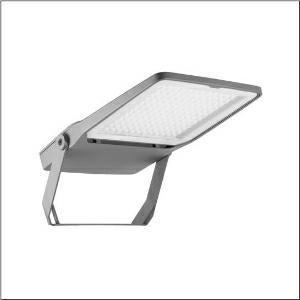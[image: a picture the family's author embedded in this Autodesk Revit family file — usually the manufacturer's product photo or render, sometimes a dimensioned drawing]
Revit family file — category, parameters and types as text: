
# Revit family: floodlight_fl_20_midi___pl61_5xa7682d2c1ac_8fda
name_source: partatom
category: Lighting Fixtures
units: mm (PartAtom-declared; Revit-internal decimal feet)

## family parameters
Cut with Voids When Loaded = No
Host = Face
Light Source = No
Part Type = Normal
Room Calculation Point = No
Round Connector Dimension = Use Diameter
Shared = No

## types (1)
- --- (1 x LED 4000K / CRI = 70 (unbekannt), 18200 lm, 4000K)
    Apparent Load = 142 VA
    CIE Flux Codes = 33 65 98 100 100
    Color Rendering = 70
    Color Temperature = 4000K
    Default Elevation = 1800 mm
    Description = Floodlight FL 20 midi, floodlight, primary light control with lens, of plastic, primary optical cover: protective disc, of toughened safety glass, transparent, light distribution: PL61, light emission: direct distribution, primary light characteristic: asymmetric, installation type: surface-mounted, LED High Power LED, rated luminous flux: 18.200 lm, light colour: 740, colour temperature: 4000K, control gear: ECG Plus, control: flexible luminous flux parameterisation, time-dependent luminous flux control, digital communication interface, power reduction, overheat protection, electronic power reduction, with terminal, 5-pole, max. 2.5mm², mains connection: 220..240V, AC, 50/60Hz, rated input power: 142W, LED unit, of diecast aluminium, powder-coated, Siteco® metallic grey (DB 702S), length: 654 mm, width: 450 mm, height: 76mm, housing frame, of diecast aluminium, powder-coated, Siteco® metallic grey (DB 702S), mounting bracket, of steel, powder-coated, Siteco® metallic grey (DB 702S), DALIprotection rating (complete): IP66, insulation class (complete): insulation class II (safety insulation), certification: CE, ENEC, VDE, protection symbol: D, permissible ambient temperature for indoor applications: -40..+40°C, permissible ambient temperature for outdoor applications: -40..+50°C, standard: DIN EN 12944, packaging unit: 1 piece

Light Distribution: PL61
    Height = 76 mm
    Lamp = 1 x LED 4000K / CRI >= 70 (unbekannt)
    Lamp Light Flux = 18200 lm
    Lamp count = 1
    Length = 672 mm
    Luminous efficacy = 128 lm/W
    Manufacturer = Siteco
    ModVariant = No
    Model = 5XA7682D2C1AC
    Number of Poles = 1
    OnlyDefault = Yes
    Power Factor = 1
    Product Name = Floodlight FL 20 midi | PL61
    Product group = floodlight | pylon top
    ProductGroupID = 6101
    Protection Class = Protection class II
    Protection Degree = IP 66
    RLX_Detail_Level = 1
    RlxData = <blob elided: 97665 chars, md5=967276a7>
    Socket = socket
    Standby Power = 0 W
    System Light Flux = 18200 lm
    System Power = 142 W
    Type Comments = factory setting: luminous flux: 100 % | dim-lin: 254 | 489 mA
    Type Image = l_1005943.jpg
    URL = http://relux.com
    VarID = @adj_142643
    Voltage = 0 V
    Weight = 0.00 kg
    Width = 450 mm

## geometry (parser evidence)
native form markers: Blend x4, Sweep x12
no freeform markers — native parametric forms only
